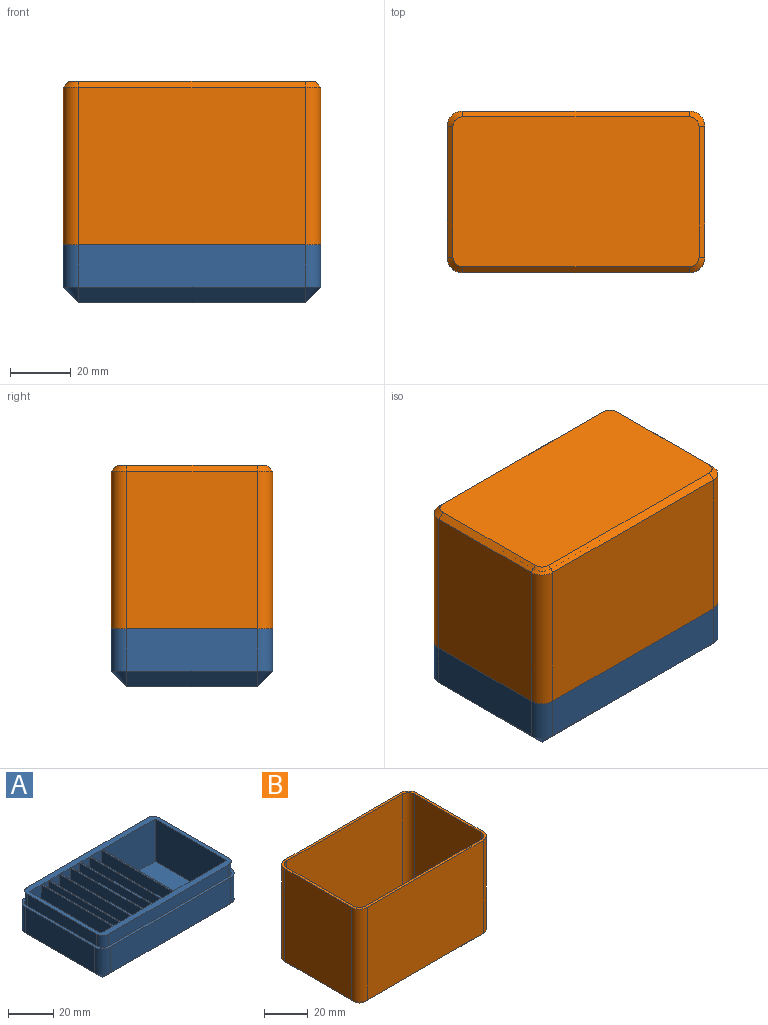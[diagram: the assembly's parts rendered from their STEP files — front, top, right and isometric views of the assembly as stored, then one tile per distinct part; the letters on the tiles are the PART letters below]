
ASSEMBLY  parts=2 mates=1
PART A: 67 faces, bbox 85.1x53.3x25.4 mm
  f0: plane 82.55x50.8mm, normal (0,0,1), area 905.2mm2, adj f1,f2,f3,f4,f5,f6,f7,f8
  f1: plane 43.18x6.35mm, normal (1,0,0), area 274.2mm2, adj f0,f2,f8,f17
  f2: cylinder r=3.81mm len=6.35mm, axis (0,0,-1), area 38mm2, adj f0,f1,f3,f17
  f3: plane 74.93x6.35mm, normal (0,1,0), area 475.8mm2, adj f0,f2,f4,f17
  f4: cylinder r=3.81mm len=6.35mm, axis (0,0,-1), area 38mm2, adj f0,f3,f5,f17
  f5: plane 43.18x6.35mm, normal (-1,0,0), area 274.2mm2, adj f0,f4,f6,f17
  f6: cylinder r=3.81mm len=6.35mm, axis (0,0,-1), area 38mm2, adj f0,f5,f7,f17
  f7: plane 74.93x6.35mm, normal (0,-1,0), area 475.8mm2, adj f0,f6,f8,f17
  f8: cylinder r=3.81mm len=6.35mm, axis (0,0,-1), area 38mm2, adj f0,f1,f7,f17
  f9: plane 43.18x13.97mm, normal (1,0,0), area 603.2mm2, adj f10,f16,f17,f63
  f10: cylinder r=5.08mm len=13.97mm, axis (0,0,-1), area 111.5mm2, adj f9,f11,f17,f65
  f11: plane 74.93x13.97mm, normal (0,1,0), area 1046.8mm2, adj f10,f12,f17,f66
  f12: cylinder r=5.08mm len=13.97mm, axis (0,0,-1), area 111.5mm2, adj f11,f13,f17,f64
  f13: plane 43.18x13.97mm, normal (-1,0,0), area 603.2mm2, adj f12,f14,f17,f62
  f14: cylinder r=5.08mm len=13.97mm, axis (0,0,-1), area 111.5mm2, adj f13,f15,f17,f60
  f15: plane 74.93x13.97mm, normal (0,-1,0), area 1046.8mm2, adj f14,f16,f17,f59
  f16: cylinder r=5.08mm len=13.97mm, axis (0,0,-1), area 111.5mm2, adj f9,f15,f17,f61
  f17: plane 85.09x53.34mm, normal (0,0,1), area 335.5mm2, adj f1,f2,f3,f4,f5,f6,f7,f8
  f18: plane 74.93x43.18mm, normal (0,0,-1), area 3235.5mm2, adj f59,f62,f63,f66
  f19: plane 33.02x22.86mm, normal (0,1,0), area 754.8mm2, adj f0,f20,f22,f23
  f20: plane 44.7x22.86mm, normal (-1,0,0), area 1021.9mm2, adj f0,f19,f21,f23
  f21: plane 33.02x22.86mm, normal (0,-1,0), area 754.8mm2, adj f0,f20,f22,f23
  f22: plane 44.7x22.86mm, normal (1,0,0), area 1021.9mm2, adj f0,f19,f21,f23
  f23: plane 44.7x33.02mm, normal (0,0,1), area 1476.1mm2, adj f19,f20,f21,f22
  f24: plane 22.86x6.6mm, normal (0,-1,0), area 151mm2, adj f0,f25,f27,f28
  f25: plane 44.7x22.86mm, normal (1,0,0), area 1021.9mm2, adj f0,f24,f26,f28
  f26: plane 22.86x6.6mm, normal (0,1,0), area 151mm2, adj f0,f25,f27,f28
  f27: plane 44.7x22.86mm, normal (-1,0,0), area 1021.9mm2, adj f0,f24,f26,f28
  f28: plane 44.7x6.6mm, normal (0,0,1), area 295.2mm2, adj f24,f25,f26,f27
  f29: plane 22.86x5.33mm, normal (0,-1,0), area 121.9mm2, adj f0,f30,f32,f33
  f30: plane 44.7x22.86mm, normal (1,0,0), area 1021.9mm2, adj f0,f29,f31,f33
  f31: plane 22.86x5.33mm, normal (0,1,0), area 121.9mm2, adj f0,f30,f32,f33
  f32: plane 44.7x22.86mm, normal (-1,0,0), area 1021.9mm2, adj f0,f29,f31,f33
  f33: plane 44.7x5.33mm, normal (0,0,1), area 238.5mm2, adj f29,f30,f31,f32
  f34: plane 22.86x4.83mm, normal (0,-1,0), area 110.3mm2, adj f0,f35,f37,f38
  f35: plane 44.7x22.86mm, normal (1,0,0), area 1021.9mm2, adj f0,f34,f36,f38
  f36: plane 22.86x4.83mm, normal (0,1,0), area 110.3mm2, adj f0,f35,f37,f38
  f37: plane 44.7x22.86mm, normal (-1,0,0), area 1021.9mm2, adj f0,f34,f36,f38
  f38: plane 44.7x4.83mm, normal (0,0,1), area 215.7mm2, adj f34,f35,f36,f37
  f39: plane 22.86x6.22mm, normal (0,-1,0), area 142.3mm2, adj f0,f40,f42,f43
  f40: plane 44.7x22.86mm, normal (1,0,0), area 1021.9mm2, adj f0,f39,f41,f43
  f41: plane 22.86x6.22mm, normal (0,1,0), area 142.3mm2, adj f0,f40,f42,f43
  f42: plane 44.7x22.86mm, normal (-1,0,0), area 1021.9mm2, adj f0,f39,f41,f43
  f43: plane 44.7x6.22mm, normal (0,0,1), area 278.2mm2, adj f39,f40,f41,f42
  f44: plane 22.86x6.22mm, normal (0,-1,0), area 142.3mm2, adj f0,f45,f47,f48
  f45: plane 44.7x22.86mm, normal (1,0,0), area 1021.9mm2, adj f0,f44,f46,f48
  f46: plane 22.86x6.22mm, normal (0,1,0), area 142.3mm2, adj f0,f45,f47,f48
  f47: plane 44.7x22.86mm, normal (-1,0,0), area 1021.9mm2, adj f0,f44,f46,f48
  f48: plane 44.7x6.22mm, normal (0,0,1), area 278.2mm2, adj f44,f45,f46,f47
  f49: plane 22.86x3.68mm, normal (0,-1,0), area 84.2mm2, adj f0,f50,f52,f53
  f50: plane 44.7x22.86mm, normal (1,0,0), area 1021.9mm2, adj f0,f49,f51,f53
  f51: plane 22.86x3.68mm, normal (0,1,0), area 84.2mm2, adj f0,f50,f52,f53
  f52: plane 44.7x22.86mm, normal (-1,0,0), area 1021.9mm2, adj f0,f49,f51,f53
  f53: plane 44.7x3.68mm, normal (0,0,1), area 164.6mm2, adj f49,f50,f51,f52
  f54: plane 22.86x7.37mm, normal (0,-1,0), area 168.4mm2, adj f0,f55,f57,f58
  f55: plane 44.7x22.86mm, normal (1,0,0), area 1021.9mm2, adj f0,f54,f56,f58
  f56: plane 22.86x7.37mm, normal (0,1,0), area 168.4mm2, adj f0,f55,f57,f58
  f57: plane 44.7x22.86mm, normal (-1,0,0), area 1021.9mm2, adj f0,f54,f56,f58
  f58: plane 44.7x7.37mm, normal (0,0,1), area 329.3mm2, adj f54,f55,f56,f57
  f59: plane 74.93x5.08mm, normal (0,-0.71,-0.71), area 538.3mm2, adj f15,f18,f60,f61
  f60: cone r=5.08mm half-angle=45deg, axis (0,0,1), area 28.7mm2, adj f14,f59,f62
  f61: cone r=5.08mm half-angle=45deg, axis (0,0,1), area 28.7mm2, adj f16,f59,f63
  f62: plane 43.18x5.08mm, normal (-0.71,0,-0.71), area 310.2mm2, adj f13,f18,f60,f64
  f63: plane 43.18x5.08mm, normal (0.71,0,-0.71), area 310.2mm2, adj f9,f18,f61,f65
  f64: cone r=5.08mm half-angle=45deg, axis (0,0,1), area 28.7mm2, adj f12,f62,f66
  f65: cone r=5.08mm half-angle=45deg, axis (0,0,1), area 28.7mm2, adj f10,f63,f66
  f66: plane 74.93x5.08mm, normal (0,0.71,-0.71), area 538.3mm2, adj f11,f18,f64,f65
PART B: 27 faces, bbox 85.1x53.3x54 mm
  f0: plane 52.07x43.18mm, normal (1,0,0), area 2248.4mm2, adj f1,f7,f8,f23
  f1: cylinder r=5.08mm len=52.07mm, axis (0,0,-1), area 415.5mm2, adj f0,f2,f8,f25
  f2: plane 74.93x52.07mm, normal (0,1,0), area 3901.6mm2, adj f1,f3,f8,f26
  f3: cylinder r=5.08mm len=52.07mm, axis (0,0,-1), area 415.5mm2, adj f2,f4,f8,f24
  f4: plane 52.07x43.18mm, normal (-1,0,0), area 2248.4mm2, adj f3,f5,f8,f22
  f5: cylinder r=5.08mm len=52.07mm, axis (0,0,-1), area 415.5mm2, adj f4,f6,f8,f20
  f6: plane 74.93x52.07mm, normal (0,-1,0), area 3901.6mm2, adj f5,f7,f8,f19
  f7: cylinder r=5.08mm len=52.07mm, axis (0,0,-1), area 415.5mm2, adj f0,f6,f8,f21
  f8: plane 85.09x53.34mm, normal (0,0,1), area 335.5mm2, adj f0,f1,f2,f3,f4,f5,f6,f7
  f9: plane 81.28x49.53mm, normal (0,0,-1), area 4017.1mm2, adj f19,f20,f21,f22,f23,f24,f25,f26
  f10: plane 52.71x43.18mm, normal (-1,0,0), area 2275.8mm2, adj f8,f11,f17,f18
  f11: cylinder r=3.81mm len=52.71mm, axis (0,0,-1), area 315.4mm2, adj f8,f10,f12,f18
  f12: plane 74.93x52.71mm, normal (0,-1,0), area 3949.2mm2, adj f8,f11,f13,f18
  f13: cylinder r=3.81mm len=52.71mm, axis (0,0,-1), area 315.4mm2, adj f8,f12,f14,f18
  f14: plane 52.71x43.18mm, normal (1,0,0), area 2275.8mm2, adj f8,f13,f15,f18
  f15: cylinder r=3.81mm len=52.71mm, axis (0,0,-1), area 315.4mm2, adj f8,f14,f16,f18
  f16: plane 74.93x52.71mm, normal (0,1,0), area 3949.2mm2, adj f8,f15,f17,f18
  f17: cylinder r=3.81mm len=52.71mm, axis (0,0,-1), area 315.4mm2, adj f8,f10,f16,f18
  f18: plane 82.55x50.8mm, normal (0,0,1), area 4181.1mm2, adj f10,f11,f12,f13,f14,f15,f16,f17
  f19: plane 74.93x1.91mm, normal (0,-0.71,-0.71), area 201.9mm2, adj f6,f9,f20,f21
  f20: cone r=5.08mm half-angle=45deg, axis (0,0,1), area 17.5mm2, adj f5,f9,f19,f22
  f21: cone r=5.08mm half-angle=45deg, axis (0,0,1), area 17.5mm2, adj f7,f9,f19,f23
  f22: plane 43.18x1.91mm, normal (-0.71,0,-0.71), area 116.3mm2, adj f4,f9,f20,f24
  f23: plane 43.18x1.91mm, normal (0.71,0,-0.71), area 116.3mm2, adj f0,f9,f21,f25
  f24: cone r=5.08mm half-angle=45deg, axis (0,0,1), area 17.5mm2, adj f3,f9,f22,f26
  f25: cone r=5.08mm half-angle=45deg, axis (0,0,1), area 17.5mm2, adj f1,f9,f23,f26
  f26: plane 74.93x1.91mm, normal (0,0.71,-0.71), area 201.9mm2, adj f2,f9,f24,f25
PLACE A t=(-1.93,-0.4,0.76)mm
PLACE B rot(axis=(1,0,0),180deg) t=(-0.3,38.41,73.79)mm
MATE fastened B.f8 <-> A.f17  axis (0,0,-1) through (1.88,-1.67,19.81)mm
